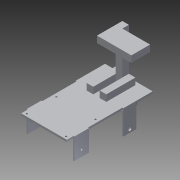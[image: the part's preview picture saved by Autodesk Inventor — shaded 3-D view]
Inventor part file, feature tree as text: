
AUTODESK INVENTOR PART (.ipt)
format: ipt  version: 2014 (Build 180170000, 170)  size: 264,192 bytes
history: native  units: mm
features: sketch x18, extrude x16, plane x4, mirror x3
ambient origin geometry x8: Origin, YZ Plane, XZ Plane, XY Plane, X Axis, Y Axis, Z Axis, Center Point
bodies: Solid1 (feature_tree)
feature tree (41):
  extrude  "Extrusion1"  Depth=20.0mm
  extrude  "Extrusion2"  Depth=20.0mm
  plane  "Work Plane1"
  mirror  "Mirror1"
  extrude  "Extrusion3"  [1 undecoded]
  extrude  "Extrusion10"  Depth=5.0mm
  sketch  "Sketch13"  dims[d26=20.0mm d28=90.0mm d29=20.0mm d31=120.0mm d34=36.0mm d35=0.0mm]
  sketch  "Sketch14"  dims[d36=55.0mm d39=120.0mm]
  plane  "Work Plane2"
  extrude  "Extrusion12"  Depth=20.0mm TaperAngle=0.0deg
  mirror  "Mirror3"
  sketch  "Sketch15"  dims[d44=7.0mm d45=20.0mm]
  extrude  "Extrusion13"  Depth=120.0mm
  mirror  "Mirror4"
  extrude  "Extrusion14"  Depth=20.0mm
  extrude  "Extrusion15"  Depth=75.0mm
  extrude  "Extrusion16"  Depth=10.0mm
  extrude  "Extrusion17"  Depth=3.0mm TaperAngle=0.0deg
  extrude  "Extrusion20"  Depth=10.0mm TaperAngle=0.0deg
  extrude  "Extrusion21"  Depth=50.0mm TaperAngle=0.0deg
  extrude  "Extrusion22"  Depth=50.0mm TaperAngle=0.0deg
  extrude  "Extrusion23"  Depth=20.0mm TaperAngle=0.0deg
  plane  "Work Plane3"
  extrude  "Extrusion24"  Depth=85.0mm TaperAngle=0.0deg
  plane  "Work Plane4"
  extrude  "Extrusion26"  [1 undecoded]
  sketch  "Sketch2"  dims[d0=20.0mm d1=20.0mm]
  sketch  "Sketch3"  dims[d2=210.0mm d3=0.0mm d4=20.0mm]
  sketch  "Sketch4"  dims[d5=100.0mm d6=0.0mm d7=-50.0mm]
  sketch  "Sketch11"  dims[d9=150.0mm d10=0.0mm d25=5.0mm]
  sketch  "Sketch18"  dims[d47=3.0mm d48=0.0mm d51=75.0mm]
  sketch  "Sketch19"  dims[d52=3.0mm d53=0.0mm d54=10.0mm]
  sketch  "Sketch20"  dims[d55=10.0mm d56=3.0mm d57=0.0mm]
  sketch  "Sketch21"  dims[d58=10.0mm d59=0.0mm d60=10.0mm d61=0.0mm]
  sketch  "Sketch22"  dims[d62=3.0mm d63=0.0mm d71=50.0mm d72=0.0mm]
  sketch  "Sketch25"  dims[d73=3.0mm d74=50.0mm d75=0.0mm]
  sketch  "Sketch26"  dims[d76=40.0mm d77=0.0mm d78=20.0mm d79=0.0mm]
  sketch  "Sketch27"  dims[d80=20.0mm d81=0.0mm d87=85.0mm d88=0.0mm]
  sketch  "Sketch28"
  sketch  "Sketch29"
  sketch  "Sketch32"
note: 2 required parameter values undecoded (feature->parameter linkage not recoverable at this tier; creation-order binding heuristic only, values carry confidence <= 0.55)
